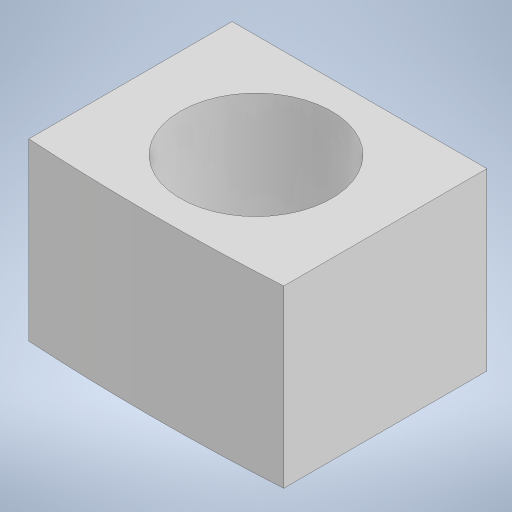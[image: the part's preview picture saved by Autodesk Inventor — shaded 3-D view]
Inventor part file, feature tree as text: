
AUTODESK INVENTOR PART (.ipt)
format: ipt  version: 2024 (Build 280153000, 153)  size: 174,592 bytes
history: native  units: mm
features: extrude x1, sketch x1
ambient origin geometry x8: Origin, YZ Plane, XZ Plane, XY Plane, X Axis, Y Axis, Z Axis, Center Point
bodies: Solid1 (feature_tree)
feature tree (2):
  extrude  "Extrusion1"  Depth=5.5mm
  sketch  "Sketch1"  dims[d0=170.0mm d1=109.0mm d2=105.5mm d3=166.5mm d4=160.0mm d5=4.75mm d6=3.25mm d7=4.0mm d8=4.0mm d9=163.25mm d10=5.5mm d11=0.0mm]
